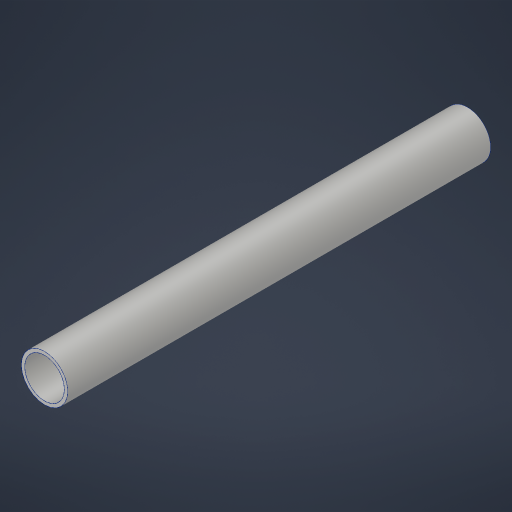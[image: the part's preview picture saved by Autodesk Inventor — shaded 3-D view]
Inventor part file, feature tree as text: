
AUTODESK INVENTOR PART (.ipt)
format: ipt  version: 2023.4 (Build 274418000, 418)  size: 167,936 bytes
history: native  units: in
note: dims shown in document units (in); Inventor stores cm internally (conversion verified against a paired STEP export)
features: extrude x1, sketch x1
ambient origin geometry x8: Origin, YZ Plane, XZ Plane, XY Plane, X Axis, Y Axis, Z Axis, Center Point
bodies: Solid1 (feature_tree)
feature tree (2):
  extrude  "Extrusion1"  Depth=8.0in
  sketch  "Sketch1"  dims[d0=0.875in d1=0.0625in d2=8.0in d3=0.0in]
